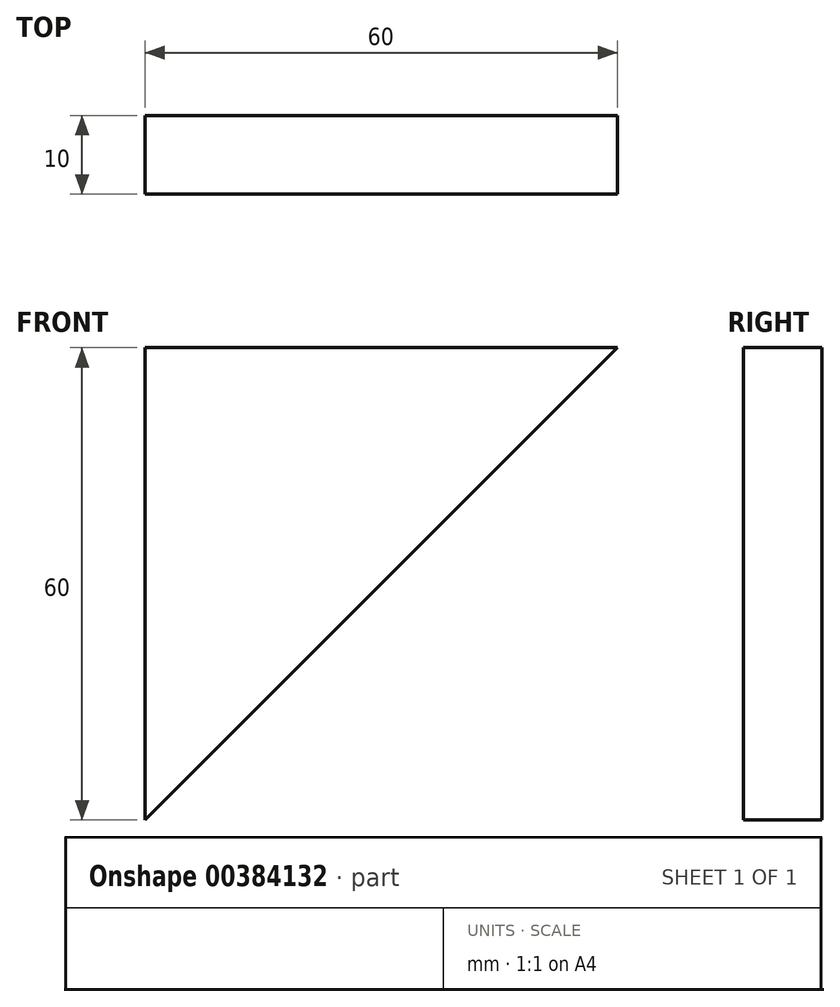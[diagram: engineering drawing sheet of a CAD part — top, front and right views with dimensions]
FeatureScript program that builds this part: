
annotation { "Feature Type Name" : "Feature", "Feature Type Description" : "" }
export const myFeature = defineFeature(function(context is Context, id is Id, definition is map)
    precondition{}
    {
        {
            var Q0;
            Q0=qCreatedBy(makeId("Front.planeOp"),FACE);
            var sketch = newSketch(context, id + "F0", { "sketchPlane" : qUnion([Q0])});
            skLineSegment(sketch, "E0.bottom", {"start": v(30, 30) * mm, "end": v(-30, 30) * mm});
            skLineSegment(sketch, "E0.right", {"start": v(-30, 30) * mm, "end": v(-30, -30) * mm});
            skPoint(sketch, "E0.middle", {"position": v(0, 0) * mm});
            skLineSegment(sketch, "E1", {"start": v(30, 30) * mm, "end": v(-30, -30) * mm});
            skPoint(sketch, "E0.left.end.orphan", {"position": v(30, -30) * mm});
            skSolve(sketch);
        }
        {
            var Q0;
            Q0=makeQuery(id+"F0.imprint","IMPRINT",FACE,{"disambiguationData":[TD([[makeQuery(id+"F0.imprint","IMPRINT",EDGE,{"derivedFrom":sQuery(id+"F0.wireOp",EDGE,"E0.bottom")}),1.0]])]});
            extrude(context, id + "F1", {"entities" : qUnion([Q0]), "depth" : 10 * mm});
        }
    });
